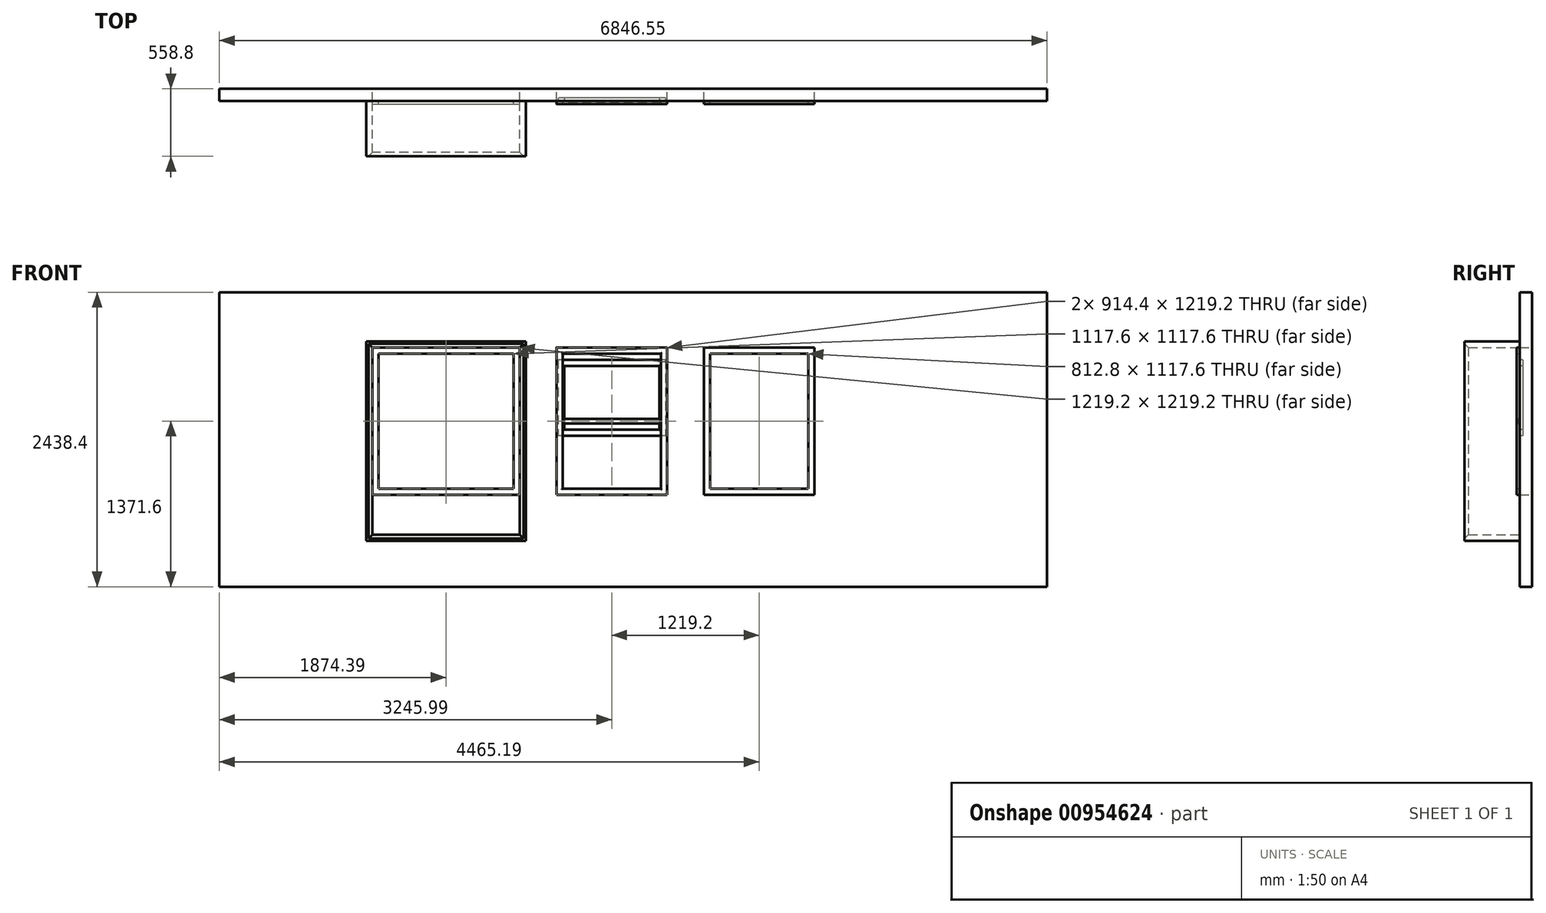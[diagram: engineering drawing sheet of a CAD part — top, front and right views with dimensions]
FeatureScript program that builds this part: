
annotation { "Feature Type Name" : "Feature", "Feature Type Description" : "" }
export const myFeature = defineFeature(function(context is Context, id is Id, definition is map)
    precondition{}
    {
        {
            var Q0;
            Q0=qCreatedBy(makeId("Front.planeOp"),FACE);
            var sketch = newSketch(context, id + "F0", { "sketchPlane" : qUnion([Q0])});
            skLineSegment(sketch, "E0.bottom", {"start": v(-609.6, 762) * mm, "end": v(609.6, 762) * mm});
            skLineSegment(sketch, "E0.top", {"start": v(-609.6, 1981.2) * mm, "end": v(609.6, 1981.2) * mm});
            skLineSegment(sketch, "E0.left", {"start": v(-609.6, 762) * mm, "end": v(-609.6, 1981.2) * mm});
            skLineSegment(sketch, "E0.right", {"start": v(609.6, 762) * mm, "end": v(609.6, 1981.2) * mm});
            skPoint(sketch, "E0.middle", {"position": v(0, 1371.6) * mm});
            skLineSegment(sketch, "E1", {"start": v(0, 762) * mm, "end": v(0, 0) * mm, "construction": true});
            skLineSegment(sketch, "E2", {"start": v(-1874.39, 0) * mm, "end": v(4972.16, 0) * mm});
            skLineSegment(sketch, "E3", {"start": v(-1874.39, 2438.4) * mm, "end": v(4972.16, 2438.4) * mm});
            skLineSegment(sketch, "E4.bottom", {"start": v(914.4, 1981.2) * mm, "end": v(1828.8, 1981.2) * mm});
            skLineSegment(sketch, "E4.top", {"start": v(914.4, 762) * mm, "end": v(1828.8, 762) * mm});
            skLineSegment(sketch, "E4.left", {"start": v(914.4, 1981.2) * mm, "end": v(914.4, 762) * mm});
            skLineSegment(sketch, "E4.right", {"start": v(1828.8, 1981.2) * mm, "end": v(1828.8, 762) * mm});
            skLineSegment(sketch, "E5.bottom", {"start": v(2133.6, 1981.2) * mm, "end": v(3048, 1981.2) * mm});
            skLineSegment(sketch, "E5.top", {"start": v(2133.6, 762) * mm, "end": v(3048, 762) * mm});
            skLineSegment(sketch, "E5.left", {"start": v(2133.6, 1981.2) * mm, "end": v(2133.6, 762) * mm});
            skLineSegment(sketch, "E5.right", {"start": v(3048, 1981.2) * mm, "end": v(3048, 762) * mm});
            skLineSegment(sketch, "E6.bottom", {"start": v(-578.24, 1950.75) * mm, "end": v(566.7, 1950.75) * mm});
            skLineSegment(sketch, "E6.top", {"start": v(-578.24, 828.95) * mm, "end": v(566.7, 828.95) * mm});
            skLineSegment(sketch, "E6.left", {"start": v(-578.24, 1950.75) * mm, "end": v(-578.24, 828.95) * mm});
            skLineSegment(sketch, "E6.right", {"start": v(566.7, 1950.75) * mm, "end": v(566.7, 828.95) * mm});
            skLineSegment(sketch, "E7.bottom", {"start": v(1062.06, 1649) * mm, "end": v(1741.82, 1649) * mm});
            skLineSegment(sketch, "E7.top", {"start": v(1062.06, 1117.02) * mm, "end": v(1741.82, 1117.02) * mm});
            skLineSegment(sketch, "E7.left", {"start": v(1062.06, 1649) * mm, "end": v(1062.06, 1117.02) * mm});
            skLineSegment(sketch, "E7.right", {"start": v(1741.82, 1649) * mm, "end": v(1741.82, 1117.02) * mm});
            skLineSegment(sketch, "E8", {"start": v(4972.16, 2438.4) * mm, "end": v(4972.16, 0) * mm});
            skLineSegment(sketch, "E9", {"start": v(-1874.39, 2438.4) * mm, "end": v(-1874.39, 0) * mm});
            skSolve(sketch);
        }
        {
            var Q0;
            Q0=makeQuery(id+"F0.imprint","IMPRINT",FACE,{"disambiguationData":[TD([[makeQuery(id+"F0.imprint","IMPRINT",EDGE,{"derivedFrom":sQuery(id+"F0.wireOp",EDGE,"E0.bottom")}),-1.0]])]});
            extrude(context, id + "F1", {"entities" : qUnion([Q0]), "depth" : 101.6 * mm, "offsetDistance" : 25.4 * mm});
        }
        {
            var Q0;
            Q0=makeQuery(id+"F1.opExtrude","CAP_FACE",FACE,{"disambiguationData":[OSD([sQuery(id+"F0.wireOp",EDGE,"E0.bottom"),sQuery(id+"F0.wireOp",EDGE,"E0.top"),sQuery(id+"F0.wireOp",EDGE,"E0.left"),sQuery(id+"F0.wireOp",EDGE,"E0.right"),sQuery(id+"F0.wireOp",EDGE,"E2"),sQuery(id+"F0.wireOp",EDGE,"E3"),sQuery(id+"F0.wireOp",EDGE,"E4.bottom"),sQuery(id+"F0.wireOp",EDGE,"E4.top"),sQuery(id+"F0.wireOp",EDGE,"E4.left"),sQuery(id+"F0.wireOp",EDGE,"E4.right"),sQuery(id+"F0.wireOp",EDGE,"E5.bottom"),sQuery(id+"F0.wireOp",EDGE,"E5.top"),sQuery(id+"F0.wireOp",EDGE,"E5.left"),sQuery(id+"F0.wireOp",EDGE,"E5.right"),sQuery(id+"F0.wireOp",EDGE,"E8"),sQuery(id+"F0.wireOp",EDGE,"E9")])],"isStart":false});
            var sketch = newSketch(context, id + "F2", { "sketchPlane" : qUnion([Q0])});
            skLineSegment(sketch, "E10.bottom", {"start": v(-609.6, 1981.2) * mm, "end": v(609.6, 1981.2) * mm});
            skLineSegment(sketch, "E10.top", {"start": v(-609.6, 431.8) * mm, "end": v(609.6, 431.8) * mm});
            skLineSegment(sketch, "E10.left", {"start": v(-609.6, 1981.2) * mm, "end": v(-609.6, 431.8) * mm});
            skLineSegment(sketch, "E10.right", {"start": v(609.6, 1981.2) * mm, "end": v(609.6, 431.8) * mm});
            skLineSegment(sketch, "E11.0", {"start": v(660.4, 2032) * mm, "end": v(660.4, 381) * mm});
            skLineSegment(sketch, "E11.1", {"start": v(-660.4, 2032) * mm, "end": v(660.4, 2032) * mm});
            skLineSegment(sketch, "E11.2", {"start": v(-660.4, 2032) * mm, "end": v(-660.4, 381) * mm});
            skLineSegment(sketch, "E11.3", {"start": v(-660.4, 381) * mm, "end": v(660.4, 381) * mm});
            skSolve(sketch);
        }
        {
            var Q0;
            Q0 = qSketchRegion(id + "F2", true);
            extrude(context, id + "F3", {"entities" : qUnion([Q0]), "depth" : 457.2 * mm, "offsetDistance" : 25.4 * mm});
        }
        {
            var Q0;
            Q0=makeQuery(id+"F1.opExtrude","CAP_FACE",FACE,{"disambiguationData":[OSD([sQuery(id+"F0.wireOp",EDGE,"E0.bottom"),sQuery(id+"F0.wireOp",EDGE,"E0.top"),sQuery(id+"F0.wireOp",EDGE,"E0.left"),sQuery(id+"F0.wireOp",EDGE,"E0.right"),sQuery(id+"F0.wireOp",EDGE,"E2"),sQuery(id+"F0.wireOp",EDGE,"E3"),sQuery(id+"F0.wireOp",EDGE,"E4.bottom"),sQuery(id+"F0.wireOp",EDGE,"E4.top"),sQuery(id+"F0.wireOp",EDGE,"E4.left"),sQuery(id+"F0.wireOp",EDGE,"E4.right"),sQuery(id+"F0.wireOp",EDGE,"E5.bottom"),sQuery(id+"F0.wireOp",EDGE,"E5.top"),sQuery(id+"F0.wireOp",EDGE,"E5.left"),sQuery(id+"F0.wireOp",EDGE,"E5.right"),sQuery(id+"F0.wireOp",EDGE,"E8"),sQuery(id+"F0.wireOp",EDGE,"E9")])],"isStart":false});
            var sketch = newSketch(context, id + "F4", { "sketchPlane" : qUnion([Q0])});
            skLineSegment(sketch, "E12.bottom", {"start": v(-609.6, 1981.2) * mm, "end": v(609.6, 1981.2) * mm});
            skLineSegment(sketch, "E12.top", {"start": v(-609.6, 762) * mm, "end": v(609.6, 762) * mm});
            skLineSegment(sketch, "E12.left", {"start": v(-609.6, 1981.2) * mm, "end": v(-609.6, 762) * mm});
            skLineSegment(sketch, "E12.right", {"start": v(609.6, 1981.2) * mm, "end": v(609.6, 762) * mm});
            skLineSegment(sketch, "E13.0", {"start": v(-558.8, 1930.4) * mm, "end": v(558.8, 1930.4) * mm});
            skLineSegment(sketch, "E13.1", {"start": v(-558.8, 1930.4) * mm, "end": v(-558.8, 812.8) * mm});
            skLineSegment(sketch, "E13.2", {"start": v(-558.8, 812.8) * mm, "end": v(558.8, 812.8) * mm});
            skLineSegment(sketch, "E13.3", {"start": v(558.8, 1930.4) * mm, "end": v(558.8, 812.8) * mm});
            skLineSegment(sketch, "E14.bottom", {"start": v(914.4, 1981.2) * mm, "end": v(1828.8, 1981.2) * mm});
            skLineSegment(sketch, "E14.top", {"start": v(914.4, 762) * mm, "end": v(1828.8, 762) * mm});
            skLineSegment(sketch, "E14.left", {"start": v(914.4, 1981.2) * mm, "end": v(914.4, 762) * mm});
            skLineSegment(sketch, "E14.right", {"start": v(1828.8, 1981.2) * mm, "end": v(1828.8, 762) * mm});
            skLineSegment(sketch, "E15.bottom", {"start": v(2133.6, 1981.2) * mm, "end": v(3048, 1981.2) * mm});
            skLineSegment(sketch, "E15.top", {"start": v(2133.6, 762) * mm, "end": v(3048, 762) * mm});
            skLineSegment(sketch, "E15.left", {"start": v(2133.6, 1981.2) * mm, "end": v(2133.6, 762) * mm});
            skLineSegment(sketch, "E15.right", {"start": v(3048, 1981.2) * mm, "end": v(3048, 762) * mm});
            skLineSegment(sketch, "E16.0", {"start": v(965.2, 1930.4) * mm, "end": v(1778, 1930.4) * mm});
            skLineSegment(sketch, "E16.1", {"start": v(965.2, 1930.4) * mm, "end": v(965.2, 812.8) * mm});
            skLineSegment(sketch, "E16.2", {"start": v(965.2, 812.8) * mm, "end": v(1778, 812.8) * mm});
            skLineSegment(sketch, "E16.3", {"start": v(1778, 1930.4) * mm, "end": v(1778, 812.8) * mm});
            skLineSegment(sketch, "E17.0", {"start": v(2184.4, 1930.4) * mm, "end": v(2997.2, 1930.4) * mm});
            skLineSegment(sketch, "E17.1", {"start": v(2184.4, 1930.4) * mm, "end": v(2184.4, 812.8) * mm});
            skLineSegment(sketch, "E17.2", {"start": v(2184.4, 812.8) * mm, "end": v(2997.2, 812.8) * mm});
            skLineSegment(sketch, "E17.3", {"start": v(2997.2, 1930.4) * mm, "end": v(2997.2, 812.8) * mm});
            skSolve(sketch);
        }
        {
            var Q0;
            Q0=makeQuery(id+"F4.imprint","IMPRINT",FACE,{"disambiguationData":[TD([[makeQuery(id+"F4.imprint","IMPRINT",EDGE,{"derivedFrom":sQuery(id+"F4.wireOp",EDGE,"E14.bottom")}),-1.0]])]});
            var Q1;
            Q1=makeQuery(id+"F4.imprint","IMPRINT",FACE,{"disambiguationData":[TD([[makeQuery(id+"F4.imprint","IMPRINT",EDGE,{"derivedFrom":sQuery(id+"F4.wireOp",EDGE,"E15.bottom")}),-1.0]])]});
            var Q2;
            Q2=makeQuery(id+"F4.imprint","IMPRINT",FACE,{"disambiguationData":[TD([[makeQuery(id+"F4.imprint","IMPRINT",EDGE,{"derivedFrom":sQuery(id+"F4.wireOp",EDGE,"E12.bottom")}),-1.0]])]});
            extrude(context, id + "F5", {"entities" : qUnion([Q0, Q1, Q2]), "depth" : 25.4 * mm, "offsetDistance" : 25.4 * mm});
        }
        {
            var Q0;
            Q0=makeQuery(id+"F5.opExtrude","CAP_EDGE",EDGE,{"disambiguationData":[OSD([sQuery(id+"F4.wireOp",EDGE,"E14.bottom")])],"isStart":false});
            var Q1;
            Q1=makeQuery(id+"F5.opExtrude","CAP_EDGE",EDGE,{"disambiguationData":[OSD([sQuery(id+"F4.wireOp",EDGE,"E14.left")])],"isStart":false});
            var Q2;
            Q2=makeQuery(id+"F5.opExtrude","CAP_FACE",FACE,{"disambiguationData":[OSD([sQuery(id+"F4.wireOp",EDGE,"E14.bottom"),sQuery(id+"F4.wireOp",EDGE,"E14.top"),sQuery(id+"F4.wireOp",EDGE,"E14.left"),sQuery(id+"F4.wireOp",EDGE,"E14.right"),sQuery(id+"F4.wireOp",EDGE,"E16.0"),sQuery(id+"F4.wireOp",EDGE,"E16.1"),sQuery(id+"F4.wireOp",EDGE,"E16.2"),sQuery(id+"F4.wireOp",EDGE,"E16.3")])],"isStart":false});
            fillet(context, id + "F6", {"entities" : qUnion([Q0, Q1, Q2]), "radius" : 6.35 * mm, "tangentPropagation" : true, "allowEdgeOverflow" : false});
        }
        {
            var Q0;
            Q0=makeQuery(id+"F5.opExtrude","CAP_FACE",FACE,{"disambiguationData":[OSD([sQuery(id+"F4.wireOp",EDGE,"E14.bottom"),sQuery(id+"F4.wireOp",EDGE,"E14.top"),sQuery(id+"F4.wireOp",EDGE,"E14.left"),sQuery(id+"F4.wireOp",EDGE,"E14.right"),sQuery(id+"F4.wireOp",EDGE,"E16.0"),sQuery(id+"F4.wireOp",EDGE,"E16.1"),sQuery(id+"F4.wireOp",EDGE,"E16.2"),sQuery(id+"F4.wireOp",EDGE,"E16.3")])],"isStart":true});
            var sketch = newSketch(context, id + "F7", { "sketchPlane" : qUnion([Q0])});
            skLineSegment(sketch, "E18", {"start": v(-1828.8, 1371.6) * mm, "end": v(-914.4, 1371.6) * mm, "construction": true});
            skLineSegment(sketch, "E19", {"start": v(-1778, 1390.65) * mm, "end": v(-965.2, 1390.65) * mm});
            skLineSegment(sketch, "E20.MirrorCS", {"start": v(-1778, 1352.55) * mm, "end": v(-965.2, 1352.55) * mm});
            skLineSegment(sketch, "E21", {"start": v(-965.2, 1390.65) * mm, "end": v(-965.2, 1352.55) * mm});
            skLineSegment(sketch, "E22", {"start": v(-1778, 1390.65) * mm, "end": v(-1778, 1352.55) * mm});
            skSolve(sketch);
        }
        {
            var Q0;
            Q0=makeQuery(id+"F7.imprint","IMPRINT",FACE,{"disambiguationData":[TD([[makeQuery(id+"F7.imprint","IMPRINT",EDGE,{"derivedFrom":sQuery(id+"F7.wireOp",EDGE,"E19")}),-1.0]])]});
            extrude(context, id + "F8", {"entities" : qUnion([Q0]), "operationType" : NewBodyOperationType.ADD, "oppositeDirection" : true, "depth" : 19.05 * mm, "offsetDistance" : 25.4 * mm});
        }
        {
            var Q0;
            Q0=makeQuery(id+"F8.opExtrude","CAP_EDGE",EDGE,{"disambiguationData":[OSD([sQuery(id+"F7.wireOp",EDGE,"E19")])],"isStart":false});
            var Q1;
            Q1=makeQuery(id+"F8.opExtrude","CAP_EDGE",EDGE,{"disambiguationData":[OSD([sQuery(id+"F7.wireOp",EDGE,"E20.MirrorCS")])],"isStart":false});
            fillet(context, id + "F9", {"entities" : qUnion([Q0, Q1]), "radius" : 6.35 * mm, "tangentPropagation" : true, "allowEdgeOverflow" : false});
        }
        {
            var Q0;
            Q0=makeQuery(id+"F3.opExtrude","CAP_EDGE",EDGE,{"disambiguationData":[OSD([sQuery(id+"F2.wireOp",EDGE,"E10.right")])],"isStart":false});
            var Q1;
            Q1=makeQuery(id+"F3.opExtrude","CAP_EDGE",EDGE,{"disambiguationData":[OSD([sQuery(id+"F2.wireOp",EDGE,"E10.bottom")])],"isStart":false});
            var Q2;
            Q2=makeQuery(id+"F3.opExtrude","CAP_EDGE",EDGE,{"disambiguationData":[OSD([sQuery(id+"F2.wireOp",EDGE,"E10.top")])],"isStart":false});
            var Q3;
            Q3=makeQuery(id+"F3.opExtrude","CAP_EDGE",EDGE,{"disambiguationData":[OSD([sQuery(id+"F2.wireOp",EDGE,"E10.left")])],"isStart":false});
            chamfer(context, id + "F10", {"entities" : qUnion([Q0, Q1, Q2, Q3]), "width" : 31.75 * mm, "tangentPropagation" : true});
        }
        {
            var Q0;
            Q0=makeQuery(id+"F8.boolean.opBoolean","MERGE",FACE,{"derivedFrom":[makeQuery(id+"F5.opExtrude","CAP_FACE",FACE,{"disambiguationData":[OSD([sQuery(id+"F4.wireOp",EDGE,"E14.bottom"),sQuery(id+"F4.wireOp",EDGE,"E14.top"),sQuery(id+"F4.wireOp",EDGE,"E14.left"),sQuery(id+"F4.wireOp",EDGE,"E14.right"),sQuery(id+"F4.wireOp",EDGE,"E16.0"),sQuery(id+"F4.wireOp",EDGE,"E16.1"),sQuery(id+"F4.wireOp",EDGE,"E16.2"),sQuery(id+"F4.wireOp",EDGE,"E16.3")])],"isStart":true}),makeQuery(id+"F8.opExtrude","CAP_FACE",FACE,{"disambiguationData":[OSD([sQuery(id+"F7.wireOp",EDGE,"E19"),sQuery(id+"F7.wireOp",EDGE,"E20.MirrorCS"),sQuery(id+"F7.wireOp",EDGE,"E21"),sQuery(id+"F7.wireOp",EDGE,"E22")])],"isStart":true})]});
            var sketch = newSketch(context, id + "F11", { "sketchPlane" : qUnion([Q0])});
            skLineSegment(sketch, "E23.bottom", {"start": v(-1816.1, 1879.6) * mm, "end": v(-927.1, 1879.6) * mm});
            skLineSegment(sketch, "E23.top", {"start": v(-1816.1, 1250.95) * mm, "end": v(-927.1, 1250.95) * mm});
            skLineSegment(sketch, "E23.left", {"start": v(-1816.1, 1879.6) * mm, "end": v(-1816.1, 1250.95) * mm});
            skLineSegment(sketch, "E23.right", {"start": v(-927.1, 1879.6) * mm, "end": v(-927.1, 1250.95) * mm});
            skLineSegment(sketch, "E24.bottom", {"start": v(-1765.3, 1828.8) * mm, "end": v(-977.9, 1828.8) * mm});
            skLineSegment(sketch, "E24.top", {"start": v(-1765.3, 1301.75) * mm, "end": v(-977.9, 1301.75) * mm});
            skLineSegment(sketch, "E24.left", {"start": v(-1765.3, 1828.8) * mm, "end": v(-1765.3, 1301.75) * mm});
            skLineSegment(sketch, "E24.right", {"start": v(-977.9, 1828.8) * mm, "end": v(-977.9, 1301.75) * mm});
            skSolve(sketch);
        }
        {
            var Q0;
            {var subQ7=sQuery(id+"F11.wireOp",EDGE,"E23.left");Q0=makeQuery(id+"F11.imprint","IMPRINT",FACE,{"disambiguationData":[TD([[makeQuery(id+"F11.imprint","IMPRINT",EDGE,{"derivedFrom":subQ7}),1.0]])]});}
            var Q1;
            {var subQ7=sQuery(id+"F11.wireOp",EDGE,"E23.right");Q1=makeQuery(id+"F11.imprint","IMPRINT",FACE,{"disambiguationData":[TD([[makeQuery(id+"F11.imprint","IMPRINT",EDGE,{"derivedFrom":subQ7}),-1.0]])]});}
            var Q2;
            {var subQ1=sQuery(id+"F11.wireOp",EDGE,"E24.top");Q2=makeQuery(id+"F11.imprint","IMPRINT",FACE,{"disambiguationData":[TD([[makeQuery(id+"F11.imprint","IMPRINT",EDGE,{"derivedFrom":subQ1}),-1.0]])]});}
            var Q3;
            {var subQ1=sQuery(id+"F11.wireOp",EDGE,"E24.bottom");Q3=makeQuery(id+"F11.imprint","IMPRINT",FACE,{"disambiguationData":[TD([[makeQuery(id+"F11.imprint","IMPRINT",EDGE,{"derivedFrom":subQ1}),1.0]])]});}
            extrude(context, id + "F12", {"entities" : qUnion([Q0, Q1, Q2, Q3]), "depth" : 25.4 * mm, "offsetDistance" : 25.4 * mm});
        }
        {
            var Q0;
            Q0=makeQuery(id+"F12.opExtrude","CAP_FACE",FACE,{"disambiguationData":[OSD([sQuery(id+"F11.wireOp",EDGE,"E23.bottom"),sQuery(id+"F11.wireOp",EDGE,"E23.top"),sQuery(id+"F11.wireOp",EDGE,"E23.left"),sQuery(id+"F11.wireOp",EDGE,"E23.right"),sQuery(id+"F11.wireOp",EDGE,"E24.bottom"),sQuery(id+"F11.wireOp",EDGE,"E24.top"),sQuery(id+"F11.wireOp",EDGE,"E24.left"),sQuery(id+"F11.wireOp",EDGE,"E24.right")])],"isStart":true});
            fillet(context, id + "F13", {"entities" : qUnion([Q0]), "radius" : 6.35 * mm, "tangentPropagation" : true, "allowEdgeOverflow" : false});
        }
    });
